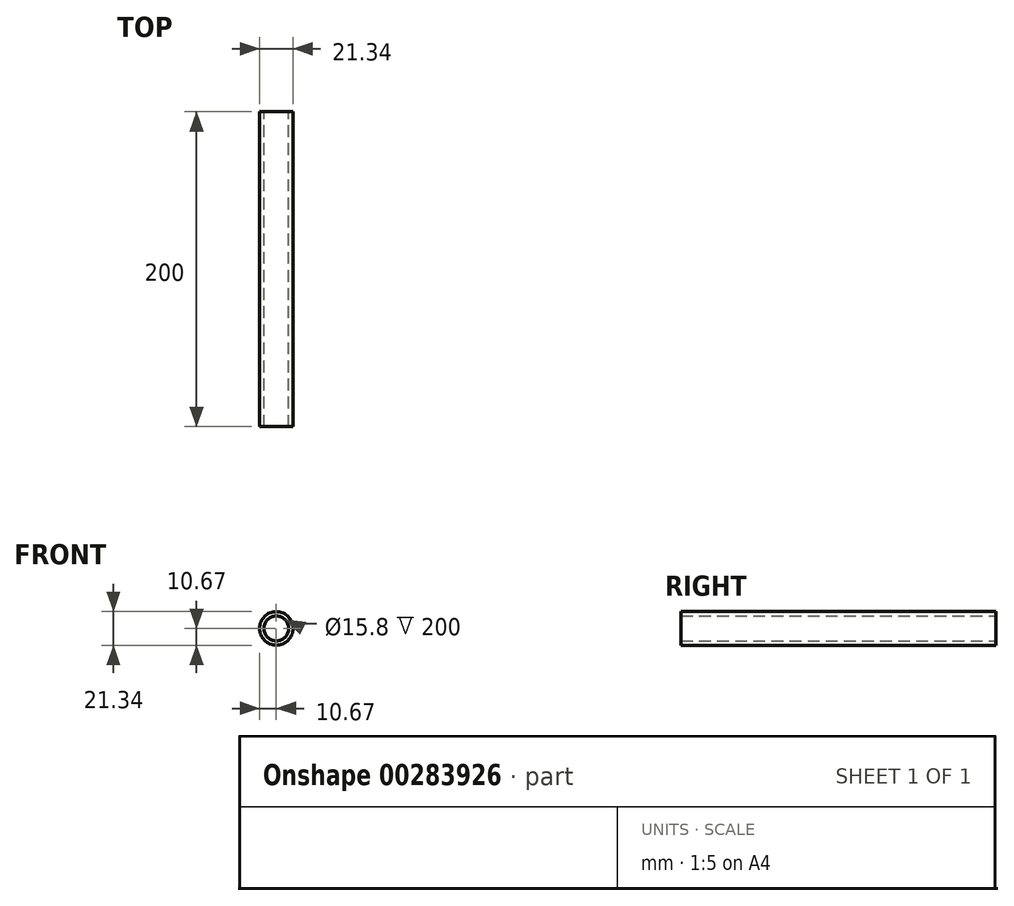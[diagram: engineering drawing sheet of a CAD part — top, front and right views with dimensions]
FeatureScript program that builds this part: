
annotation { "Feature Type Name" : "Feature", "Feature Type Description" : "" }
export const myFeature = defineFeature(function(context is Context, id is Id, definition is map)
    precondition{}
    {
        {
            var Q0;
            Q0=qCreatedBy(makeId("Front.planeOp"),FACE);
            var sketch = newSketch(context, id + "F0", { "sketchPlane" : qUnion([Q0])});
            skCircle(sketch, "E0", {"center": v(0, 0) * mm, "radius": 7.9 * mm});
            skCircle(sketch, "E1", {"center": v(0, 0) * mm, "radius": 10.67 * mm});
            skSolve(sketch);
        }
        {
            var Q0;
            Q0=qSketchRegion(id+"F0",true);
            extrude(context, id + "F1", {"entities" : qUnion([Q0]), "endBound" : BoundingType.SYMMETRIC, "depth" : 200 * mm});
        }
    });
